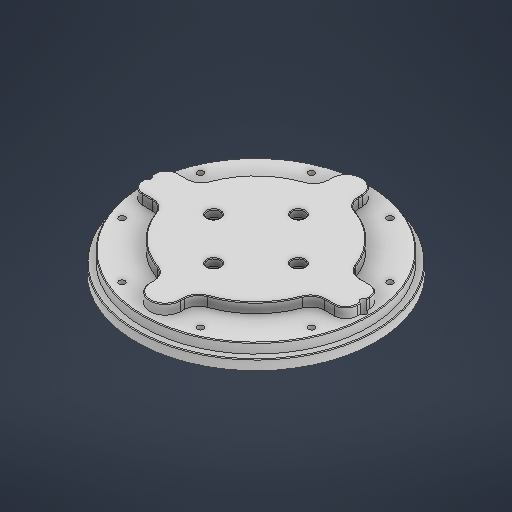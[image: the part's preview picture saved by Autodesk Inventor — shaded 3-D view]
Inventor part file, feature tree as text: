
AUTODESK INVENTOR PART (.ipt)
format: ipt  version: 2025 (Build 290162000, 162)  size: 413,696 bytes
history: native  units: mm
features: sketch x7, extrude x3, hole x3, pattern_circular x2, imported_body x1, mirror x1, chamfer x1, fillet x1
ambient origin geometry x8: Origin, YZ Plane, XZ Plane, XY Plane, X Axis, Y Axis, Z Axis, Center Point
bodies: Solid1 (feature_tree)
feature tree (19):
  imported_body  "Base"
  extrude  "Clover"  Depth=84.5mm
  hole  "Plunger Mount Holes"  [1 undecoded]
  pattern_circular  "Circular Pattern1"  Count=11  [1 undecoded]
  hole  "Seal Ring Holes"  [1 undecoded]
  pattern_circular  "Circular Pattern2"  [2 undecoded]
  hole  "Plate Mounting Holes"  [1 undecoded]
  mirror  "Mirror1"
  extrude  "Key Shape"  Depth=8.0mm
  extrude  "Bolt Recess"  Depth=10.0mm
  chamfer  "Chamfer1"  Distance=21.8mm
  fillet  "Fillet1"  Radius=10.0mm
  sketch  "Sketch1"  dims[d1=80.0mm d2=84.5mm]
  sketch  "Sketch2"  dims[d3=7.0mm d4=7.0mm]
  sketch  "Sketch3"  dims[d5=0.5mm]
  sketch  "Sketch4"  dims[d6=0.5mm]
  sketch  "Sketch5"  dims[d7=0.5mm]
  sketch  "Sketch6"  dims[d8=0.5mm]
  sketch  "Sketch7"  dims[d9=90.0deg d10=110.0mm d14=90.0deg d15=8.0mm d16=25.0mm d17=76.0mm d19=10.0mm d20=21.8mm d22=64.1mm d23=10.0mm d24=7.0mm d25=0.0mm d26=5.5mm d27=6.0mm d28=9.0mm d29=5.0mm d30=90.0deg d31=8.0mm d32=20.594885mm d33=59.9mm d35=40.0mm d36=360.0deg d38=4.4mm d39=6.0mm d40=9.0mm d41=7.2mm d42=90.0deg d43=8.0mm d44=20.594885mm d45=145.0mm d46=22.5deg d47=80.0mm d48=360.0deg d50=4.4mm d51=6.0mm d52=4.0mm d53=2.0mm d54=90.0deg d55=8.0mm d56=20.594885mm d57=81.0mm d58=35.0mm d59=1.5mm d60=0.0mm d61=20.0mm d62=6.0mm d63=0.0mm d64=0.5mm d65=2.0mm d66=45.0deg d67=4.0mm d68=10.9mm d69=8.0mm]
note: 6 required parameter values undecoded (feature->parameter linkage not recoverable at this tier; creation-order binding heuristic only, values carry confidence <= 0.55)
